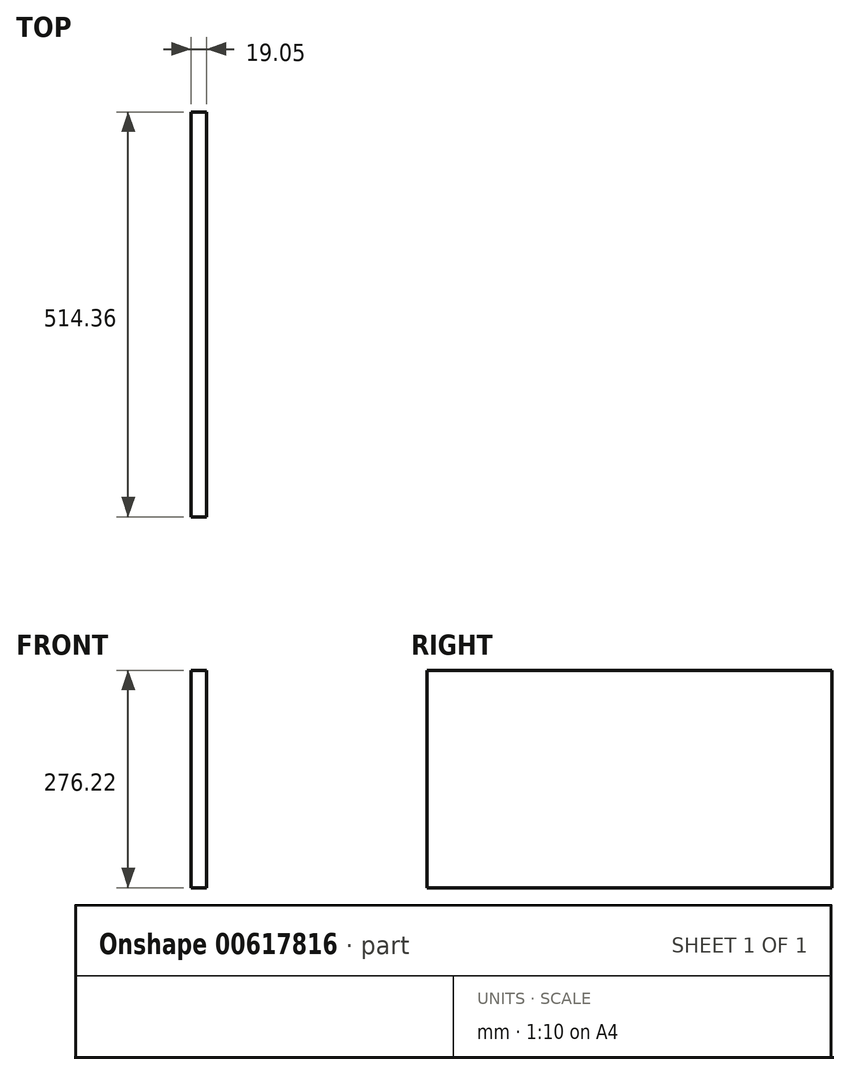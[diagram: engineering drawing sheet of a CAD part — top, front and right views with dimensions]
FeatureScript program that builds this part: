
annotation { "Feature Type Name" : "Feature", "Feature Type Description" : "" }
export const myFeature = defineFeature(function(context is Context, id is Id, definition is map)
    precondition{}
    {
        {
            var Q0;
            Q0=qCreatedBy(makeId("Right.planeOp"),FACE);
            var sketch = newSketch(context, id + "F0", { "sketchPlane" : qUnion([Q0])});
            skLineSegment(sketch, "E0.bottom", {"start": v(257.18, 138.11) * mm, "end": v(-257.18, 138.11) * mm});
            skLineSegment(sketch, "E0.top", {"start": v(257.18, -138.11) * mm, "end": v(-257.18, -138.11) * mm});
            skLineSegment(sketch, "E0.left", {"start": v(257.18, 138.11) * mm, "end": v(257.18, -138.11) * mm});
            skLineSegment(sketch, "E0.right", {"start": v(-257.18, 138.11) * mm, "end": v(-257.18, -138.11) * mm});
            skPoint(sketch, "E0.middle", {"position": v(0, 0) * mm});
            skSolve(sketch);
        }
        {
            var Q0;
            Q0=makeQuery(id+"F0.imprint","IMPRINT",FACE,{"disambiguationData":[TD([[makeQuery(id+"F0.imprint","IMPRINT",EDGE,{"derivedFrom":sQuery(id+"F0.wireOp",EDGE,"E0.bottom")}),1.0]])]});
            extrude(context, id + "F1", {"entities" : qUnion([Q0]), "depth" : 19.05 * mm, "offsetDistance" : 25.4 * mm});
        }
    });
